# Revit family: EBR-L-180-xxx-840-T
name_source: partatom
category: Oprawy oświetleniowe
revit_build: Autodesk Revit 2017 (Build: 20190507_1515(x64)
units: mm (PartAtom-declared; Revit-internal decimal feet)

## family parameters
Numer OmniClass = 23.80.70.11
Obiekt nadrzędny = Powierzchnia
Punkt obliczania pomieszczeń = Nie
Tnij formami wycięć po wczytaniu = Nie
Typ części = Normalny
Tytuł OmniClass = Luminaries for Internal Lighting
Współdzielony = Nie
Wymiar okrągłego złącza = Użyj średnicy
Źródło światła = Tak

## types (4) — shared parameters
Emituj kształt widoczny w renderingu = Nie
Emituj z długości prostokąta = 156 mm  [stored 0.511811 ft]
Emituj z szerokości prostokąta = 1524 mm  [stored 5 ft]
Filtr koloru = 16777215
Kod zespołu = D5020200
Lampa = LED
Odchylenie kierunku = 90.00°
Plik sieci fotometrycznej = EBR-L 2801870-840 T.IES
Producent = RIDI Leuchten GmbH
URL = www.ridi.de
Zmiana temperatury barwowej przyciemniania lampy = <Brak>
brand = RIDI
conformity mark = CE
electrical safety class = 1
height = 100 mm  [stored 0.328084 ft]
ingress protection (IP) code = IP20
length = 1549 mm  [stored 5.08202 ft]
nominal frequency = 50-60Hz
nominal voltage = 230
voltage type (AC, DC, UC) = AC
weight = 7 kg
width = 185 mm  [stored 0.606955 ft]
zero-valued in all types: Domyślna rzędna

## per-type parameters (varying)
| type | Model | Obciążenie pozorne | rated input power |
| EBR-L 180/620-840 T | 0850106 | 48 VA | 48 |
| EBR-L 180/620-840 T-DALI | 0860106 | 48 VA | 48 |
| EBR-L 180/935-840 T | 0850610 | 70 VA | 70 |
| EBR-L 180/935-840 T-DALI | 0860610 | 70 VA | 70 |

note: column(s) folded — value = type name in every type: product name

note: [stored X ft] marks values corroborated as IEEE doubles in the binary element streams (Revit-internal decimal feet)
